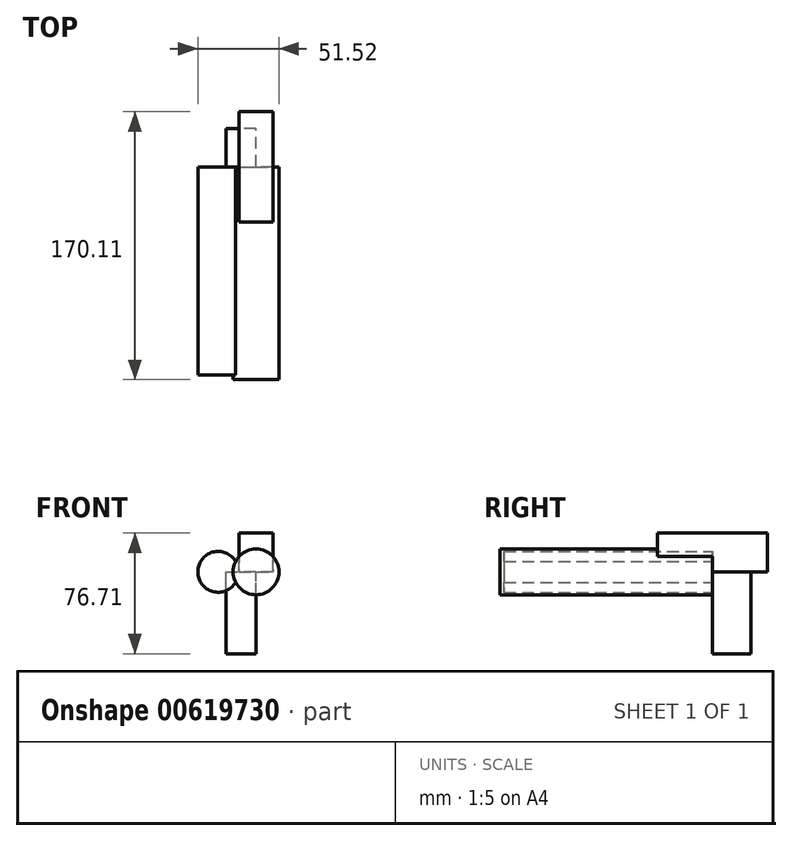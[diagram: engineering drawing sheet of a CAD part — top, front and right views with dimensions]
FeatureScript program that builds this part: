
annotation { "Feature Type Name" : "Feature", "Feature Type Description" : "" }
export const myFeature = defineFeature(function(context is Context, id is Id, definition is map)
    precondition{}
    {
        {
            var Q0;
            Q0=qCreatedBy(makeId("Front.planeOp"),FACE);
            var sketch = newSketch(context, id + "F0", { "sketchPlane" : qUnion([Q0])});
            skCircle(sketch, "E0", {"center": v(0, 0) * mm, "radius": 14.53 * mm});
            skSolve(sketch);
        }
        {
            var Q0;
            Q0=makeQuery(id+"F0.imprint","IMPRINT",FACE,{"disambiguationData":[TD([[makeQuery(id+"F0.imprint","IMPRINT",EDGE,{"derivedFrom":sQuery(id+"F0.wireOp",EDGE,"E0")}),1.0]])]});
            extrude(context, id + "F1", {"entities" : qUnion([Q0]), "depth" : 135.13 * mm, "offsetDistance" : 25.4 * mm});
        }
        {
            var Q0;
            Q0=qCreatedBy(makeId("Top.planeOp"),FACE);
            var sketch = newSketch(context, id + "F2", { "sketchPlane" : qUnion([Q0])});
            skLineSegment(sketch, "E1.bottom", {"start": v(-10.8, 34.98) * mm, "end": v(10.8, 34.98) * mm});
            skLineSegment(sketch, "E1.top", {"start": v(-10.8, -34.98) * mm, "end": v(10.8, -34.98) * mm});
            skLineSegment(sketch, "E1.left", {"start": v(-10.8, 34.98) * mm, "end": v(-10.8, -34.98) * mm});
            skLineSegment(sketch, "E1.right", {"start": v(10.8, 34.98) * mm, "end": v(10.8, -34.98) * mm});
            skPoint(sketch, "E1.middle", {"position": v(0, 0) * mm});
            skSolve(sketch);
        }
        {
            var Q0;
            Q0=makeQuery(id+"F2.imprint","IMPRINT",FACE,{"disambiguationData":[TD([[makeQuery(id+"F2.imprint","IMPRINT",EDGE,{"derivedFrom":sQuery(id+"F2.wireOp",EDGE,"E1.bottom")}),-1.0]])]});
            extrude(context, id + "F3", {"entities" : qUnion([Q0]), "operationType" : NewBodyOperationType.ADD, "depth" : 24.64 * mm, "offsetDistance" : 25.4 * mm});
        }
        {
            var Q0;
            Q0=qCreatedBy(makeId("Top.planeOp"),FACE);
            var sketch = newSketch(context, id + "F4", { "sketchPlane" : qUnion([Q0])});
            skLineSegment(sketch, "E2", {"start": v(0, 0) * mm, "end": v(0, 24.33) * mm});
            skLineSegment(sketch, "E3", {"start": v(0, 24.33) * mm, "end": v(-19.11, 24.33) * mm});
            skLineSegment(sketch, "E4", {"start": v(-19.11, 24.33) * mm, "end": v(-19.11, 3.46) * mm});
            skLineSegment(sketch, "E5", {"start": v(-19.11, 3.46) * mm, "end": v(-19.11, 0) * mm});
            skLineSegment(sketch, "E6", {"start": v(-19.11, 0) * mm, "end": v(0, 0) * mm});
            skSolve(sketch);
        }
        {
            var Q0;
            Q0=makeQuery(id+"F4.imprint","IMPRINT",FACE,{"disambiguationData":[TD([[makeQuery(id+"F4.imprint","IMPRINT",EDGE,{"derivedFrom":sQuery(id+"F4.wireOp",EDGE,"E2")}),1.0]])]});
            extrude(context, id + "F5", {"entities" : qUnion([Q0]), "operationType" : NewBodyOperationType.ADD, "oppositeDirection" : true, "depth" : 52.07 * mm, "offsetDistance" : 25.4 * mm});
        }
        {
            var Q0;
            Q0=qCreatedBy(makeId("Front.planeOp"),FACE);
            var sketch = newSketch(context, id + "F6", { "sketchPlane" : qUnion([Q0])});
            skCircle(sketch, "E7", {"center": v(-24.02, 0) * mm, "radius": 12.98 * mm});
            skSolve(sketch);
        }
        {
            var Q0;
            Q0=makeQuery(id+"F6.imprint","IMPRINT",FACE,{"disambiguationData":[TD([[makeQuery(id+"F6.imprint","IMPRINT",EDGE,{"derivedFrom":sQuery(id+"F6.wireOp",EDGE,"E7")}),1.0]])]});
            extrude(context, id + "F7", {"entities" : qUnion([Q0]), "operationType" : NewBodyOperationType.ADD, "depth" : 132.33 * mm, "offsetDistance" : 25.4 * mm});
        }
    });
